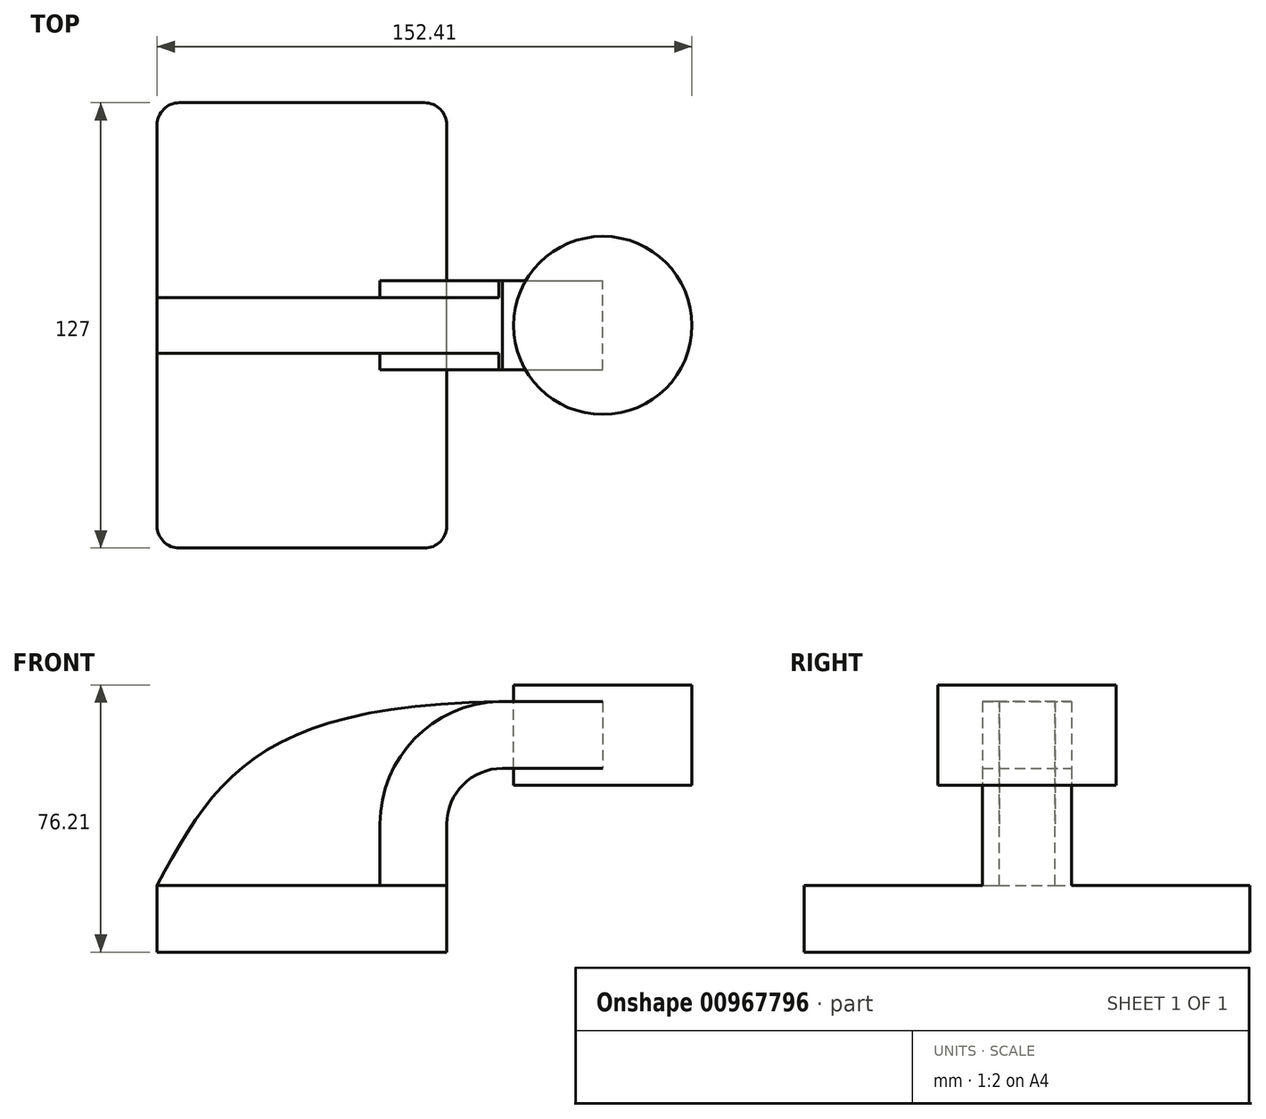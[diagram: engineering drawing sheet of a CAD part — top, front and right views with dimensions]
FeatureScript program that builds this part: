
annotation { "Feature Type Name" : "Feature", "Feature Type Description" : "" }
export const myFeature = defineFeature(function(context is Context, id is Id, definition is map)
    precondition{}
    {
        {
            var Q0;
            Q0=qCreatedBy(makeId("Front.planeOp"),FACE);
            var sketch = newSketch(context, id + "F0", { "sketchPlane" : qUnion([Q0])});
            skLineSegment(sketch, "E0.bottom", {"start": v(41.28, -9.52) * mm, "end": v(-41.28, -9.53) * mm});
            skLineSegment(sketch, "E0.top", {"start": v(41.28, 9.53) * mm, "end": v(-41.28, 9.53) * mm});
            skLineSegment(sketch, "E0.left", {"start": v(41.28, -9.52) * mm, "end": v(41.28, 9.53) * mm});
            skLineSegment(sketch, "E0.right", {"start": v(-41.28, -9.52) * mm, "end": v(-41.28, 9.53) * mm});
            skPoint(sketch, "E0.middle", {"position": v(0, 0) * mm});
            skLineSegment(sketch, "E1.bottom", {"start": v(111.12, 38.1) * mm, "end": v(60.33, 38.1) * mm});
            skLineSegment(sketch, "E1.top", {"start": v(111.12, 66.68) * mm, "end": v(60.33, 66.68) * mm});
            skLineSegment(sketch, "E1.left", {"start": v(111.12, 38.1) * mm, "end": v(111.12, 66.68) * mm});
            skLineSegment(sketch, "E1.right", {"start": v(60.32, 38.1) * mm, "end": v(60.32, 66.67) * mm});
            skPoint(sketch, "E1.middle", {"position": v(85.72, 52.39) * mm});
            skLineSegment(sketch, "E2", {"start": v(41.28, 9.53) * mm, "end": v(41.28, 27) * mm});
            skArc(sketch, "E3", {"start": v(41.27, 27) * mm, "mid": v(45.92, 38.23) * mm, "end": v(57.15, 42.88) * mm});
            skLineSegment(sketch, "E4", {"start": v(57.15, 42.88) * mm, "end": v(85.73, 42.88) * mm});
            skLineSegment(sketch, "E5.0", {"start": v(57.15, 61.93) * mm, "end": v(85.72, 61.93) * mm});
            skArc(sketch, "E5.1", {"start": v(22.23, 27) * mm, "mid": v(32.45, 51.7) * mm, "end": v(57.15, 61.93) * mm});
            skLineSegment(sketch, "E5.2", {"start": v(22.23, 9.53) * mm, "end": v(22.23, 27) * mm});
            skLineSegment(sketch, "E6", {"start": v(85.73, 61.93) * mm, "end": v(85.73, 42.88) * mm});
            skLineSegment(sketch, "E7", {"start": v(85.72, 38.1) * mm, "end": v(85.72, 42.88) * mm});
            skLineSegment(sketch, "E8", {"start": v(85.72, 61.93) * mm, "end": v(85.72, 66.68) * mm});
            skFitSpline(sketch, "E9", {"points": [v(-41.28, 9.53) * mm, v(57.15, 61.93) * mm], "startDerivative": vector(49.73, 93.07) * mm, "endDerivative": vector(206.3, 2.65) * mm});
            skSolve(sketch);
        }
        {
            var Q0;
            Q0=makeQuery(id+"F0.imprint","IMPRINT",FACE,{"disambiguationData":[TD([[makeQuery(id+"F0.imprint","IMPRINT",EDGE,{"derivedFrom":sQuery(id+"F0.wireOp",EDGE,"E0.bottom")}),-1.0]])]});
            extrude(context, id + "F1", {"entities" : qUnion([Q0]), "endBound" : BoundingType.SYMMETRIC, "depth" : 127 * mm, "offsetDistance" : 25.4 * mm});
        }
        {
            var Q0;
            {var subQ1=sQuery(id+"F0.wireOp",EDGE,"E2");Q0=makeQuery(id+"F0.imprint","IMPRINT",FACE,{"disambiguationData":[TD([[makeQuery(id+"F0.imprint","IMPRINT",EDGE,{"derivedFrom":subQ1}),1.0]])]});}
            var Q1;
            {var subQ5=sQuery(id+"F0.wireOp",EDGE,"E6");Q1=makeQuery(id+"F0.imprint","IMPRINT",FACE,{"disambiguationData":[TD([[makeQuery(id+"F0.imprint","IMPRINT",EDGE,{"derivedFrom":subQ5}),-1.0]])]});}
            extrude(context, id + "F2", {"entities" : qUnion([Q0, Q1]), "operationType" : NewBodyOperationType.ADD, "endBound" : BoundingType.SYMMETRIC, "depth" : 25.4 * mm, "offsetDistance" : 25.4 * mm});
        }
        {
            var Q0;
            {var subQ3=sQuery(id+"F0.wireOp",EDGE,"E5.2");Q0=makeQuery(id+"F0.imprint","IMPRINT",FACE,{"disambiguationData":[TD([[makeQuery(id+"F0.imprint","IMPRINT",EDGE,{"derivedFrom":subQ3}),1.0]])]});}
            extrude(context, id + "F3", {"entities" : qUnion([Q0]), "operationType" : NewBodyOperationType.ADD, "endBound" : BoundingType.SYMMETRIC, "depth" : 15.88 * mm, "offsetDistance" : 25.4 * mm});
        }
        {
            var Q0;
            {var subQ0=sQuery(id+"F0.wireOp",EDGE,"E1.left");Q0=makeQuery(id+"F0.imprint","IMPRINT",FACE,{"disambiguationData":[TD([[makeQuery(id+"F0.imprint","IMPRINT",EDGE,{"derivedFrom":subQ0}),1.0]])]});}
            var Q1;
            Q1=sQuery(id+"F0.wireOp",EDGE,"E6");
            revolve(context, id + "F4", {"surfaceOperationType" : NewSurfaceOperationType.NEW, "entities" : qUnion([Q0]), "axis" : qUnion([Q1]), "revolveType" : RevolveType.FULL});
        }
        {
            var Q0;
            Q0=makeQuery(id+"F1.opExtrude","CAP_EDGE",EDGE,{"disambiguationData":[OSD([sQuery(id+"F0.wireOp",EDGE,"E0.left")])],"isStart":false});
            var Q1;
            Q1=makeQuery(id+"F1.opExtrude","CAP_EDGE",EDGE,{"disambiguationData":[OSD([sQuery(id+"F0.wireOp",EDGE,"E0.right")])],"isStart":false});
            var Q2;
            Q2=makeQuery(id+"F1.opExtrude","CAP_EDGE",EDGE,{"disambiguationData":[OSD([sQuery(id+"F0.wireOp",EDGE,"E0.left")])],"isStart":true});
            var Q3;
            Q3=makeQuery(id+"F1.opExtrude","CAP_EDGE",EDGE,{"disambiguationData":[OSD([sQuery(id+"F0.wireOp",EDGE,"E0.right")])],"isStart":true});
            fillet(context, id + "F5", {"entities" : qUnion([Q0, Q1, Q2, Q3]), "radius" : 6.35 * mm, "tangentPropagation" : true, "allowEdgeOverflow" : false});
        }
    });
